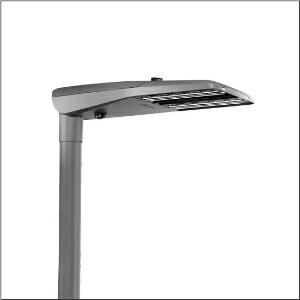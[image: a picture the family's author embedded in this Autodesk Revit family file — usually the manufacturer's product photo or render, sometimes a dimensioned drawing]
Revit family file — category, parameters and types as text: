
# Revit family: streetlight_sl_11_iq_midi___st1_2p1_0_5xc3g51y08me_d530
name_source: partatom
category: Lighting Fixtures
units: mm (PartAtom-declared; Revit-internal decimal feet)

## family parameters
Cut with Voids When Loaded = No
Host = Face
Light Source = No
Part Type = Normal
Room Calculation Point = No
Round Connector Dimension = Use Diameter
Shared = No

## types (1)
- --- (1 x LED, 17750 lm, 122.7 W, 3000K)
    Apparent Load = 123 VA
    CIE Flux Codes = 31 68 95 100 100
    Color Rendering = 70
    Color Temperature = 3000K
    Default Elevation = 1800 mm
    Description = Streetlight SL 11 iQ midi, mast luminaire, primary light control with 3 zone facetted reflector, of plastic, silver coated, highly specular, primary optical cover: cover, of PMMA, transparent, light distribution: ST1.2P1.0, light emission: direct distribution, primary light characteristic: asymmetric, installation type: post-top, side-entry, LED, High Power LED, rated luminous flux: 17.750lm, luminous efficacy: 145lm/W, light colour: 730, colour temperature: 3000K, control: presetting dimming logarithmic, Street-Remote, Auto-Match, Temp-Guard, Lumen-Switch, Night-Set, Smart-Wire, Light-Fading, Desk-Remote (wireless, voltage-free reading and setting of iQ features in the workshop via application-optimized NFC function/RFID function), optimised constant luminous flux control (CLO 2.0), with cable H07RN-F 5x 1.5mm², mains connection: 230..240V, AC, 50/60Hz, connection cable pre-assembled, cable length: 12,5m, start of lifetime: 123W, end of service life: 130W, reduction: 56W, luminaire housing, of diecast aluminium, powder-coated, Siteco® metallic grey (DB 702S), please order mast flange separately, inclination adjustable without tools: 0°, 5°, 10°, 15° (post-top) | 0°, -5°, -10°, -15° (side-entry), sealing non-destructively replaceable, multi-level sealing system, length: 780mm, width: 376mm, height: 118mm, mast flange for spigot size: 42mm (side-entry): 5XC10008XM4, 60/48mm (side-entry/post-top): 5XC10108XM2, 76/60mm (side-entry/post-top): 5XC10108XM1, equipment: Power, Smart Interface below and above, protection rating (complete): IP66, insulation class (complete): insulation class II (safety insulation), certification: CE, ENEC, VDE, UKCA, impact resistance: IK09, permissible operating ambient temperature for outdoor applications: -25..+50°C, standard-compliant lighting for roads and squares, Environmental Product Declaration (EPD) tested and certified by an independent institute, packaging unit: 1 piece

Light Distribution: ST1.2P1.0
    Height = 118 mm
    Lamp = 1 x LED
    Lamp Light Flux = 17750 lm
    Lamp Power = 122.7 W
    Lamp count = 1
    Length = 780 mm
    Luminous efficacy = 145 lm/W
    Manufacturer = Siteco
    ModVariant = No
    Model = 5XC3G51Y08ME
    Number of Poles = 1
    OnlyDefault = Yes
    Power Factor = 1
    Product Name = Streetlight SL 11 iQ midi | ST1.2P1.0
    Product group = mast luminaire | pylon top
    ProductGroupID = 6100
    Protection Class = Protection class II
    Protection Degree = IP 66
    RLX_Detail_Level = 1
    RLX_Emergency_Light_Flux = 0 lm
    RLX_Emergency_Type = 0
    RLX_Emergency_Type_DB = No
    RlxData = <blob elided: 69649 chars, md5=c5971572>
    Socket = socket
    Standby Power = 0 W
    System Light Flux = 17750 lm
    System Power = 123 W
    Type Comments = factory setting: luminous flux: 100 % | dim-lin: 254 | 553 mA
    Type Image = l_1004429.jpg
    URL = http://relux.com
    VarID = @adj_082377
    Voltage = 0 V
    Weight = 0.00 kg
    Width = 376 mm

## geometry (parser evidence)
native form markers: Blend x4, Sweep x8
no freeform markers — native parametric forms only
